# Revit family: QF_Kienle_VXE41
name_source: partatom
category: Sonderausstattung
units: mm (PartAtom-declared; Revit-internal decimal feet)

## family parameters
Arbeitsebenenbasiert = Ja
Beim Laden mit Abzugskörper schneiden = Nein
Bemaßung runder Anschluss = Durchmesser verwenden
Beschriftungsausrichtung beibehalten = Nein
Gemeinsam genutzt = Nein
Immer vertikal = Ja
OmniClass-Nummer = 23.40.40.14.17
OmniClass-Titel = Food Cooking Equipment
Raumberechnungspunkt = Nein
Schneiden in Ansichten zulassen = Nein
Teiletyp = Normal

## types (1)
- 3NAC - 400 V - 50 Hz
    Anzahl der Pole = 3
    Beschreibung = Fritteuse (1 Becken à 18-23 Liter), Einbaumodell
    CE Kennzeichnung = Ja
    Fehlstromschutzschalter Typ = A
    Frequenz = 50 Hz
    Gewicht = 37.00 kg
    Hersteller = Kienle
    Höhe = 570 mm  [stored 1.87008 ft]
    IP Schutzart = 65
    Kosten = 0 $
    Latente Abwärme Belastung = 13300 W
    Länge Gerätebreite = 404 mm  [stored 1.32546 ft]
    Modell = VXE41
    Phasen = 3
    Restfeuchte der Abluft = 19570
    Sensible Abwärme Belastung = 1710 W
    Spannung = 400 V
    Stecker System = CEE 32
    Tiefe = 675 mm  [stored 2.21457 ft]
    URL = https://www.kienle-fritteusen.de
    Vorgabe-Ansicht = 0 mm  [stored 0 ft]
    Warnhinweise = W017 / W012 (ISO 7010)
    Watt Leistung = 15000 W

note: [stored X ft] marks values corroborated as IEEE doubles in the binary element streams (Revit-internal decimal feet)
